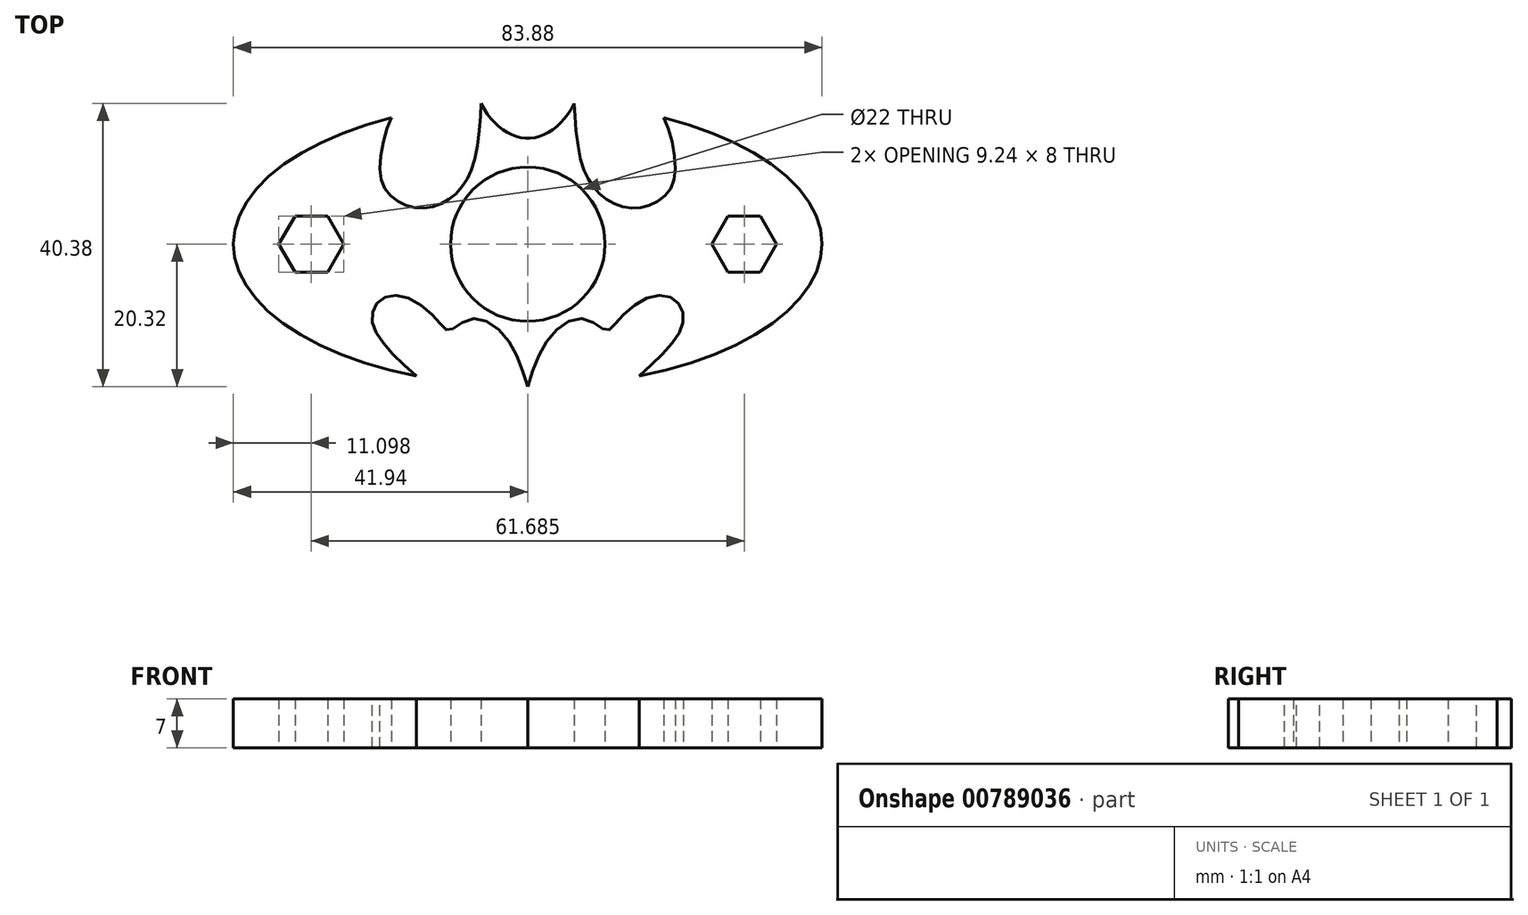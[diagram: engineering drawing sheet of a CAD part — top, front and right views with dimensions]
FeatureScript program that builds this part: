
annotation { "Feature Type Name" : "Feature", "Feature Type Description" : "" }
export const myFeature = defineFeature(function(context is Context, id is Id, definition is map)
    precondition{}
    {
        {
            var Q0;
            Q0=qCreatedBy(makeId("Top.planeOp"),FACE);
            var sketch = newSketch(context, id + "F0", { "sketchPlane" : qUnion([Q0])});
            skCircle(sketch, "E0", {"center": v(0, 0) * mm, "radius": 11 * mm});
            skCircle(sketch, "E1", {"center": v(0, 0) * mm, "radius": 38 * mm, "construction": true});
            skFitSpline(sketch, "E2", {"points": [v(-19.39, 18.02) * mm, v(-21.03, 11.33) * mm, v(-20.1, 7.51) * mm, v(-17.37, 5.53) * mm, v(-14.33, 5.16) * mm, v(-11.4, 6.26) * mm, v(-9.15, 8.46) * mm, v(-7.48, 12.33) * mm, v(-6.63, 20.06) * mm], "startDerivative": vector(-15.36, -27.41) * mm, "endDerivative": vector(1.38, 36.58) * mm});
            skEllipticalArc(sketch, "E3", {});
            skFitSpline(sketch, "E4", {"points": [v(0, -20.32) * mm, v(-3.23, -13.17) * mm, v(-8.12, -10.65) * mm, v(-11.23, -12.28) * mm, v(-12.56, -11.24) * mm, v(-17, -7.69) * mm, v(-20.85, -7.84) * mm, v(-22.18, -10.35) * mm, v(-20.85, -13.76) * mm, v(-15.88, -18.8) * mm], "startDerivative": vector(-16.39, 52.54) * mm, "endDerivative": vector(40.33, -36.14) * mm});
            skEllipticalArc(sketch, "E5", {});
            skPoint(sketch, "E5.centerSnap0", {"position": v(0, 20.32) * mm});
            skFitSpline(sketch, "E6.MirrorCS", {"points": [v(19.39, 18.02) * mm, v(21.03, 11.33) * mm, v(20.1, 7.51) * mm, v(17.37, 5.53) * mm, v(14.33, 5.16) * mm, v(11.4, 6.26) * mm, v(9.15, 8.46) * mm, v(7.48, 12.33) * mm, v(6.63, 20.06) * mm], "startDerivative": vector(15.36, -27.41) * mm, "endDerivative": vector(-1.38, 36.58) * mm});
            skFitSpline(sketch, "E7.MirrorCS", {"points": [v(0, -20.32) * mm, v(3.23, -13.17) * mm, v(8.12, -10.65) * mm, v(11.23, -12.28) * mm, v(12.56, -11.24) * mm, v(17, -7.69) * mm, v(20.85, -7.84) * mm, v(22.18, -10.35) * mm, v(20.85, -13.76) * mm, v(15.88, -18.8) * mm], "startDerivative": vector(16.39, 52.54) * mm, "endDerivative": vector(-40.33, -36.14) * mm});
            skEllipticalArc(sketch, "E8.trimOffspring", {});
            skCircle(sketch, "E9.cCircle", {"center": v(-30.84, 0) * mm, "radius": 4 * mm, "construction": true});
            skLineSegment(sketch, "E9.0", {"start": v(-28.53, 4) * mm, "end": v(-26.22, 0) * mm});
            skLineSegment(sketch, "E9.1", {"start": v(-26.22, 0) * mm, "end": v(-28.53, -4) * mm});
            skLineSegment(sketch, "E9.2", {"start": v(-28.53, -4) * mm, "end": v(-33.15, -4) * mm});
            skLineSegment(sketch, "E9.3", {"start": v(-33.15, -4) * mm, "end": v(-35.46, 0) * mm});
            skLineSegment(sketch, "E9.4", {"start": v(-35.46, 0) * mm, "end": v(-33.15, 4) * mm});
            skLineSegment(sketch, "E9.5", {"start": v(-33.15, 4) * mm, "end": v(-28.53, 4) * mm});
            skPoint(sketch, "E9.0.midPoint", {"position": v(-27.38, 2) * mm});
            skLineSegment(sketch, "E10.MirrorCS", {"start": v(35.46, 0) * mm, "end": v(33.15, 4) * mm});
            skPoint(sketch, "E11.MirrorP", {"position": v(27.38, 2) * mm});
            skLineSegment(sketch, "E12.MirrorCS", {"start": v(28.53, -4) * mm, "end": v(33.15, -4) * mm});
            skLineSegment(sketch, "E13.MirrorCS", {"start": v(33.15, -4) * mm, "end": v(35.46, 0) * mm});
            skLineSegment(sketch, "E14.MirrorCS", {"start": v(33.15, 4) * mm, "end": v(28.53, 4) * mm});
            skCircle(sketch, "E15.MirrorC", {"center": v(30.84, 0) * mm, "radius": 4 * mm, "construction": true});
            skLineSegment(sketch, "E16.MirrorCS", {"start": v(28.53, 4) * mm, "end": v(26.22, 0) * mm});
            skLineSegment(sketch, "E17.MirrorCS", {"start": v(26.22, 0) * mm, "end": v(28.53, -4) * mm});
            const initialGuessF0  = {"E3": [0, 0, 1, 0, 0.04193682778295196, 0.020318691293085327, 5.100809109250265, 1.0901618052611255], "E5": [0, 0.027689702808856964, 0, -1, 0.012582238763570786, 0.008334474322871295, 5.363573613358935, 0.9196116938206522], "E8.trimOffspring": [0, 0, 1, 0, 0.04193682778295196, 0.020318691293085327, 2.0514308483286676, 4.323968851519114]};
            skSetInitialGuess(sketch, initialGuessF0);
            skSolve(sketch);
        }
        {
            var Q0;
            Q0 = qSketchRegion(id + "F0", true);
            extrude(context, id + "F1", {"entities" : qUnion([Q0]), "endBound" : BoundingType.SYMMETRIC, "depth" : 7 * mm, "offsetDistance" : 25 * mm});
        }
    });
